# Revit family: PRD_FrankeWS_JntrlUnits_SiriusMultiPurposeSink_BS323N,BS324N
name_source: partatom
category: Plumbing Fixtures
revit_build: Autodesk Revit 2018 (Build: 20190510_1515(x64)
units: mm (PartAtom-declared; Revit-internal decimal feet)

## family parameters
Cut with Voids When Loaded = No
Host = Face
OmniClass Number = 23.45.05.14.14
OmniClass Title = Sinks/Lavatories
Part Type = Normal
Room Calculation Point = No
Round Connector Dimension = Use Diameter
Shared = No

## types (2) — shared parameters
AssetType = Fixed
Category = Pr_40_20_96_44, Janitorial sinks
Color = Stainless steel
DrainSize = DN 40 (1 1/2 inch.)
DurationUnit = year
Features = stainless steel, 0.80 mm, satin finished, inset mounting, 670x281x520 mm (WxHxD)
Finish = Satin finished
FinishAndMaterial = Stainless steel 1.4301
Form = Stainless steel multi purpose sink
GrossWeight = 7.10 kg
IfcExportAs = IfcSanitaryTerminalType
IfcExportType = SINK
IntegralAccessories = incl. washer and clamps for inset mounting
Manufacturer = KWC Group AG
ManufacturerName = KWC Group AG
ManufacturerURL = www.kwc.com
Material = Stainless steel
NBSDescription = Janitorial units
NBSReference = 45-35-70/401
NetWeight = 6.10 kg
NominalDepth = 520 mm  [stored 1.70604 ft]
NominalHeight = 281 mm  [stored 0.921916 ft]
NominalWidth = 670 mm  [stored 2.19816 ft]
OutletSize = DN 40 (1 1/2 inch.)
ProductInformation = https://pim.kwc.com
Shape = Rectangular
SinkMaterial = PRD_AR_StainlessSteel_SatinFinished
SinkMounting = CounterTop
SinkType = Other
Size = 670 x 520 x 281mm
URL = www.kwc.com
Uniclass2015Code = Pr_40_20_96_44
Uniclass2015Title = Janitorial sinks
Uniclass2015Version = Products v1.10
Version = 1
WarrantyDurationUnit = year
WasteSize = 40  [stored 0.131234 ft]
WaterSupplyOverflowAndWasteHolesOverflow = Stand pipe overflow
WaterSupplyOverflowAndWasteHolesWaste = Right-Back-Corner
zero-valued in all types: Default Elevation

## per-type parameters (varying)
| type | BIMObjectName | Description | ModelNumber | Name | Taphole | WaterSupplyOverflowAndWasteHolesWaterSupply |
| BS324N | PRD_AR_JanitorialUnits_SiriusMultiPurposeSink_BS324N | SIRIUS washtrough for inset mounting, stainless steel, satin finished surface, material thickness of trough 0.8 mm / side panels 1.2 mm, seamlessly welded, front panel without rubbing board, 75 mm tap landing, no tap holes, no overflow, right hand waste, G 1 1/2 B plastic standpipe strainer, includes seals and fixing claws for inset mounting. | 2030045757 | Sirius multi purpose sink BS324N | No | No tapholes |
| BS323N | PRD_AR_JanitorialUnits_SiriusMultiPurposeSink_BS323N | SIRIUS washtrough for inset mounting, stainless steel, satin finished surface, material thickness of trough 0.8 mm / side panels 1.2 mm, seamlessly welded, front panel without rubbing board, 75 mm tap landing, with 35 mm tap hole, no overflow, right hand drain, G 1 1/2 B plastic standpipe strainer, includes seals and fixing claws for inset mounting. | 2030045756 | Sirius multi purpose sink BS323N | Yes | Single tap hole, middle, 35 mm |

note: column(s) folded — value = type name in every type: Model, ModelReference

note: [stored X ft] marks values corroborated as IEEE doubles in the binary element streams (Revit-internal decimal feet)

## geometry (parser evidence)
native form markers: Sweep x6
no freeform markers — native parametric forms only
